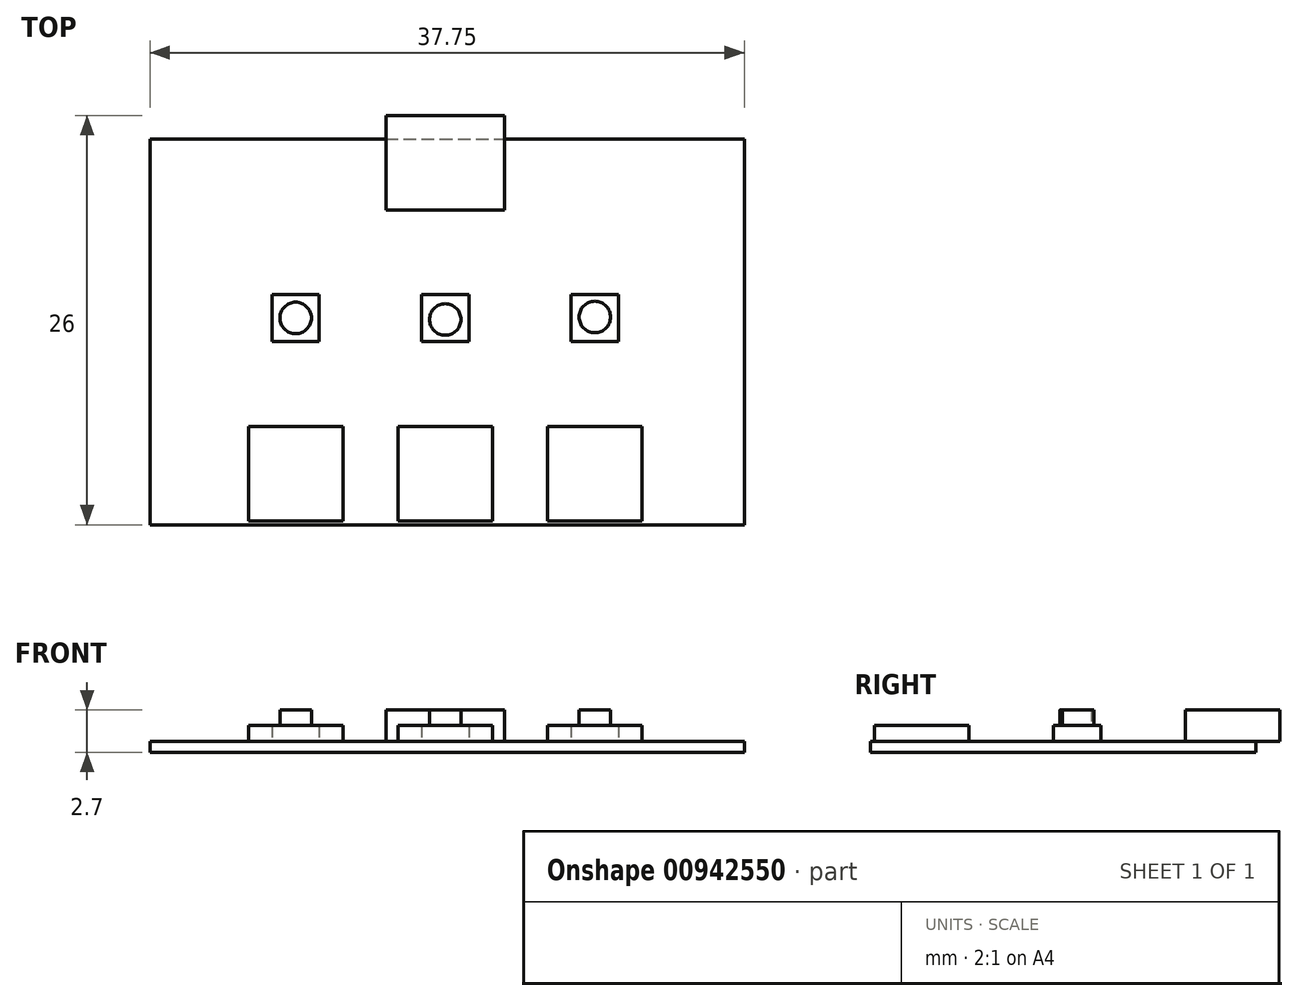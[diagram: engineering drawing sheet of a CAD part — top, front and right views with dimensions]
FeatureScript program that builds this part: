
annotation { "Feature Type Name" : "Feature", "Feature Type Description" : "" }
export const myFeature = defineFeature(function(context is Context, id is Id, definition is map)
    precondition{}
    {
        {
            var Q0;
            Q0=qCreatedBy(makeId("Top.planeOp"),FACE);
            var sketch = newSketch(context, id + "F0", { "sketchPlane" : qUnion([Q0])});
            skLineSegment(sketch, "E0.bottom", {"start": v(0, 0) * mm, "end": v(37.75, 0) * mm});
            skLineSegment(sketch, "E0.top", {"start": v(0, 24.5) * mm, "end": v(37.75, 24.5) * mm});
            skLineSegment(sketch, "E0.left", {"start": v(0, 0) * mm, "end": v(0, 24.5) * mm});
            skLineSegment(sketch, "E0.right", {"start": v(37.75, 0) * mm, "end": v(37.75, 24.5) * mm});
            skSolve(sketch);
        }
        {
            var Q0;
            Q0=makeQuery(id+"F0.imprint","IMPRINT",FACE,{"disambiguationData":[TD([[makeQuery(id+"F0.imprint","IMPRINT",EDGE,{"derivedFrom":sQuery(id+"F0.wireOp",EDGE,"E0.bottom")}),1.0]])]});
            extrude(context, id + "F1", {"entities" : qUnion([Q0]), "depth" : .7 * mm, "offsetDistance" : 25 * mm});
        }
        {
            var Q0;
            Q0=makeQuery(id+"F1.opExtrude","CAP_FACE",FACE,{"disambiguationData":[OSD([sQuery(id+"F0.wireOp",EDGE,"E0.bottom"),sQuery(id+"F0.wireOp",EDGE,"E0.top"),sQuery(id+"F0.wireOp",EDGE,"E0.left"),sQuery(id+"F0.wireOp",EDGE,"E0.right")])],"isStart":false});
            var sketch = newSketch(context, id + "F2", { "sketchPlane" : qUnion([Q0])});
            skLineSegment(sketch, "E1.bottom", {"start": v(6.25, 6.25) * mm, "end": v(12.25, 6.25) * mm});
            skLineSegment(sketch, "E1.top", {"start": v(6.25, 0.25) * mm, "end": v(12.25, 0.25) * mm});
            skLineSegment(sketch, "E1.left", {"start": v(6.25, 6.25) * mm, "end": v(6.25, 0.25) * mm});
            skLineSegment(sketch, "E1.right", {"start": v(12.25, 6.25) * mm, "end": v(12.25, 0.25) * mm});
            skLineSegment(sketch, "E2.1.0.0", {"start": v(15.75, 6.25) * mm, "end": v(21.75, 6.25) * mm});
            skLineSegment(sketch, "E2.1.0.1", {"start": v(15.75, 0.25) * mm, "end": v(21.75, 0.25) * mm});
            skLineSegment(sketch, "E2.1.0.2", {"start": v(21.75, 6.25) * mm, "end": v(21.75, 0.25) * mm});
            skLineSegment(sketch, "E2.1.0.3", {"start": v(15.75, 6.25) * mm, "end": v(15.75, 0.25) * mm});
            skLineSegment(sketch, "E2.2.0.0", {"start": v(25.25, 6.25) * mm, "end": v(31.25, 6.25) * mm});
            skLineSegment(sketch, "E2.2.0.1", {"start": v(25.25, 0.25) * mm, "end": v(31.25, 0.25) * mm});
            skLineSegment(sketch, "E2.2.0.2", {"start": v(31.25, 6.25) * mm, "end": v(31.25, 0.25) * mm});
            skLineSegment(sketch, "E2.2.0.3", {"start": v(25.25, 6.25) * mm, "end": v(25.25, 0.25) * mm});
            skLineSegment(sketch, "E2.direction1", {"start": v(6.25, 6.25) * mm, "end": v(15.75, 6.25) * mm, "construction": true});
            skLineSegment(sketch, "E3", {"start": v(0, 3.25) * mm, "end": v(9.25, 3.25) * mm, "construction": true});
            skSolve(sketch);
        }
        {
            var Q0;
            Q0=makeQuery(id+"F2.imprint","IMPRINT",FACE,{"disambiguationData":[TD([[makeQuery(id+"F2.imprint","IMPRINT",EDGE,{"derivedFrom":sQuery(id+"F2.wireOp",EDGE,"E1.bottom")}),-1.0]])]});
            var Q1;
            Q1=makeQuery(id+"F2.imprint","IMPRINT",FACE,{"disambiguationData":[TD([[makeQuery(id+"F2.imprint","IMPRINT",EDGE,{"derivedFrom":sQuery(id+"F2.wireOp",EDGE,"E2.1.0.0")}),-1.0]])]});
            var Q2;
            Q2=makeQuery(id+"F2.imprint","IMPRINT",FACE,{"disambiguationData":[TD([[makeQuery(id+"F2.imprint","IMPRINT",EDGE,{"derivedFrom":sQuery(id+"F2.wireOp",EDGE,"E2.2.0.0")}),-1.0]])]});
            extrude(context, id + "F3", {"entities" : qUnion([Q0, Q1, Q2]), "operationType" : NewBodyOperationType.ADD, "depth" : 1 * mm, "offsetDistance" : 25 * mm});
        }
        {
            var Q0;
            Q0=makeQuery(id+"F1.opExtrude","CAP_FACE",FACE,{"disambiguationData":[OSD([sQuery(id+"F0.wireOp",EDGE,"E0.bottom"),sQuery(id+"F0.wireOp",EDGE,"E0.top"),sQuery(id+"F0.wireOp",EDGE,"E0.left"),sQuery(id+"F0.wireOp",EDGE,"E0.right")])],"isStart":false});
            var sketch = newSketch(context, id + "F4", { "sketchPlane" : qUnion([Q0])});
            skLineSegment(sketch, "E4", {"start": v(0, 13) * mm, "end": v(9.25, 13) * mm, "construction": true});
            skLineSegment(sketch, "E5.bottom", {"start": v(7.75, 14.64) * mm, "end": v(10.75, 14.64) * mm});
            skLineSegment(sketch, "E5.top", {"start": v(7.75, 11.64) * mm, "end": v(10.75, 11.64) * mm});
            skLineSegment(sketch, "E5.left", {"start": v(7.75, 14.64) * mm, "end": v(7.75, 11.64) * mm});
            skLineSegment(sketch, "E5.right", {"start": v(10.75, 14.64) * mm, "end": v(10.75, 11.64) * mm});
            skLineSegment(sketch, "E6.1.0.0", {"start": v(17.25, 14.64) * mm, "end": v(17.25, 11.64) * mm});
            skLineSegment(sketch, "E6.1.0.1", {"start": v(17.25, 14.64) * mm, "end": v(20.25, 14.64) * mm});
            skLineSegment(sketch, "E6.1.0.2", {"start": v(17.25, 11.64) * mm, "end": v(20.25, 11.64) * mm});
            skLineSegment(sketch, "E6.1.0.3", {"start": v(20.25, 14.64) * mm, "end": v(20.25, 11.64) * mm});
            skLineSegment(sketch, "E6.2.0.0", {"start": v(26.75, 14.64) * mm, "end": v(26.75, 11.64) * mm});
            skLineSegment(sketch, "E6.2.0.1", {"start": v(26.75, 14.64) * mm, "end": v(29.75, 14.64) * mm});
            skLineSegment(sketch, "E6.2.0.2", {"start": v(26.75, 11.64) * mm, "end": v(29.75, 11.64) * mm});
            skLineSegment(sketch, "E6.2.0.3", {"start": v(29.75, 14.64) * mm, "end": v(29.75, 11.64) * mm});
            skLineSegment(sketch, "E6.direction1", {"start": v(7.75, 11.64) * mm, "end": v(17.25, 11.64) * mm, "construction": true});
            skSolve(sketch);
        }
        {
            var Q0;
            Q0=makeQuery(id+"F4.imprint","IMPRINT",FACE,{"disambiguationData":[TD([[makeQuery(id+"F4.imprint","IMPRINT",EDGE,{"derivedFrom":sQuery(id+"F4.wireOp",EDGE,"E5.bottom")}),-1.0]])]});
            var Q1;
            Q1=makeQuery(id+"F4.imprint","IMPRINT",FACE,{"disambiguationData":[TD([[makeQuery(id+"F4.imprint","IMPRINT",EDGE,{"derivedFrom":sQuery(id+"F4.wireOp",EDGE,"E6.1.0.0")}),1.0]])]});
            var Q2;
            Q2=makeQuery(id+"F4.imprint","IMPRINT",FACE,{"disambiguationData":[TD([[makeQuery(id+"F4.imprint","IMPRINT",EDGE,{"derivedFrom":sQuery(id+"F4.wireOp",EDGE,"E6.2.0.0")}),1.0]])]});
            extrude(context, id + "F5", {"entities" : qUnion([Q0, Q1, Q2]), "operationType" : NewBodyOperationType.ADD, "depth" : 1 * mm, "offsetDistance" : 25 * mm});
        }
        {
            var Q0;
            Q0=makeQuery(id+"F5.opExtrude","CAP_FACE",FACE,{"disambiguationData":[OSD([sQuery(id+"F4.wireOp",EDGE,"E5.bottom"),sQuery(id+"F4.wireOp",EDGE,"E5.top"),sQuery(id+"F4.wireOp",EDGE,"E5.left"),sQuery(id+"F4.wireOp",EDGE,"E5.right")])],"isStart":false});
            var sketch = newSketch(context, id + "F6", { "sketchPlane" : qUnion([Q0])});
            skCircle(sketch, "E7", {"center": v(9.25, 13.14) * mm, "radius": 1 * mm});
            skPoint(sketch, "E7.centerSnap0", {"position": v(7.75, 13.14) * mm});
            skCircle(sketch, "E8", {"center": v(18.75, 13.05) * mm, "radius": 1 * mm});
            skCircle(sketch, "E9", {"center": v(28.25, 13.2) * mm, "radius": 1 * mm});
            skSolve(sketch);
        }
        {
            var Q0;
            Q0=makeQuery(id+"F6.imprint","IMPRINT",FACE,{"disambiguationData":[TD([[makeQuery(id+"F6.imprint","IMPRINT",EDGE,{"derivedFrom":sQuery(id+"F6.wireOp",EDGE,"E7")}),1.0]])]});
            var Q1;
            Q1=makeQuery(id+"F6.imprint","IMPRINT",FACE,{"disambiguationData":[TD([[makeQuery(id+"F6.imprint","IMPRINT",EDGE,{"derivedFrom":sQuery(id+"F6.wireOp",EDGE,"E8")}),1.0]])]});
            var Q2;
            Q2=makeQuery(id+"F6.imprint","IMPRINT",FACE,{"disambiguationData":[TD([[makeQuery(id+"F6.imprint","IMPRINT",EDGE,{"derivedFrom":sQuery(id+"F6.wireOp",EDGE,"E9")}),1.0]])]});
            extrude(context, id + "F7", {"entities" : qUnion([Q0, Q1, Q2]), "operationType" : NewBodyOperationType.ADD, "depth" : 1 * mm, "offsetDistance" : 25 * mm});
        }
        {
            var Q0;
            Q0=makeQuery(id+"F1.opExtrude","CAP_FACE",FACE,{"disambiguationData":[OSD([sQuery(id+"F0.wireOp",EDGE,"E0.bottom"),sQuery(id+"F0.wireOp",EDGE,"E0.top"),sQuery(id+"F0.wireOp",EDGE,"E0.left"),sQuery(id+"F0.wireOp",EDGE,"E0.right")])],"isStart":false});
            var sketch = newSketch(context, id + "F8", { "sketchPlane" : qUnion([Q0])});
            skLineSegment(sketch, "E10.bottom", {"start": v(22.5, 20) * mm, "end": v(15, 20) * mm});
            skLineSegment(sketch, "E10.top", {"start": v(22.5, 26) * mm, "end": v(15, 26) * mm});
            skLineSegment(sketch, "E10.left", {"start": v(22.5, 20) * mm, "end": v(22.5, 26) * mm});
            skLineSegment(sketch, "E10.right", {"start": v(15, 20) * mm, "end": v(15, 26) * mm});
            skSolve(sketch);
        }
        {
            var Q0;
            {var subQ0=sQuery(id+"F8.wireOp",EDGE,"E10.bottom");Q0=makeQuery(id+"F8.imprint","IMPRINT",FACE,{"disambiguationData":[TD([[makeQuery(id+"F8.imprint","IMPRINT",EDGE,{"derivedFrom":subQ0}),-1.0]])]});}
            var Q1;
            {var subQ0=sQuery(id+"F8.wireOp",EDGE,"E10.top");Q1=makeQuery(id+"F8.imprint","IMPRINT",FACE,{"disambiguationData":[TD([[makeQuery(id+"F8.imprint","IMPRINT",EDGE,{"derivedFrom":subQ0}),1.0]])]});}
            extrude(context, id + "F9", {"entities" : qUnion([Q0, Q1]), "operationType" : NewBodyOperationType.ADD, "depth" : 2 * mm, "offsetDistance" : 25 * mm});
        }
    });
